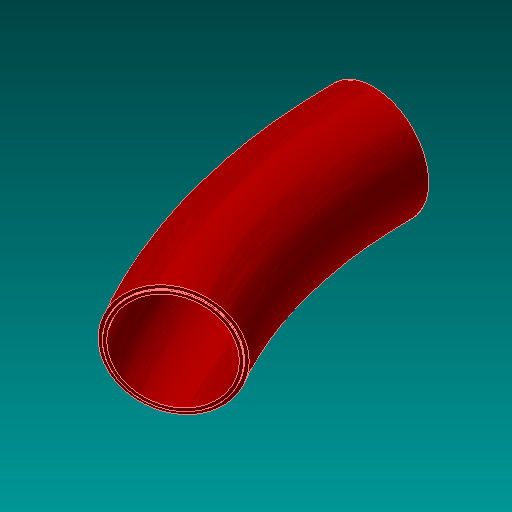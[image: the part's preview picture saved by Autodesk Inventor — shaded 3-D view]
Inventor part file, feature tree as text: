
AUTODESK INVENTOR PART (.ipt)
format: ipt  version: 2017.3 (Build 213257000, 257)  size: 235,008 bytes
history: native  units: in
note: dims shown in document units (in); Inventor stores cm internally (conversion verified against a paired STEP export)
features: revolve x3, extrude x3, sketch x2, plane x1, fillet x1, chamfer x1
ambient origin geometry x8: Origin, YZ Plane, XZ Plane, XY Plane, X Axis, Y Axis, Z Axis, Center Point
bodies: Solid1 (feature_tree)
feature tree (11):
  sketch  "Sketch1"  dims[d0=28.5in d1=32.5in]
  revolve  "Revolution1"  [1 undecoded]
  sketch  "Sketch11"  dims[d2=160.0in d3=30.0deg d37=30.48in d38=33.5in d39=0.25in d40=0.0in d41=0.25in d42=0.0in d43=0.0034in d44=0.0312in d45=0.0312in d46=0.125in d47=45.0deg d48=0.25in d49=0.0137in d50=30.5in d51=0.5in d52=0.0in]
  extrude  "Extrusion10"  TaperAngle=30.0deg  [1 undecoded]
  extrude  "Extrusion11"  Depth=160.0in
  revolve  "Revolution2"  [1 undecoded]
  plane  "Work Plane3"
  revolve  "Revolution3"  [1 undecoded]
  extrude  "Extrusion12"  Depth=160.0in TaperAngle=0.0deg
  fillet  "Fillet3"  Radius=0.0034in
  chamfer  "Chamfer3"  Distance=0.0312in
note: 4 required parameter values undecoded (feature->parameter linkage not recoverable at this tier; creation-order binding heuristic only, values carry confidence <= 0.55)